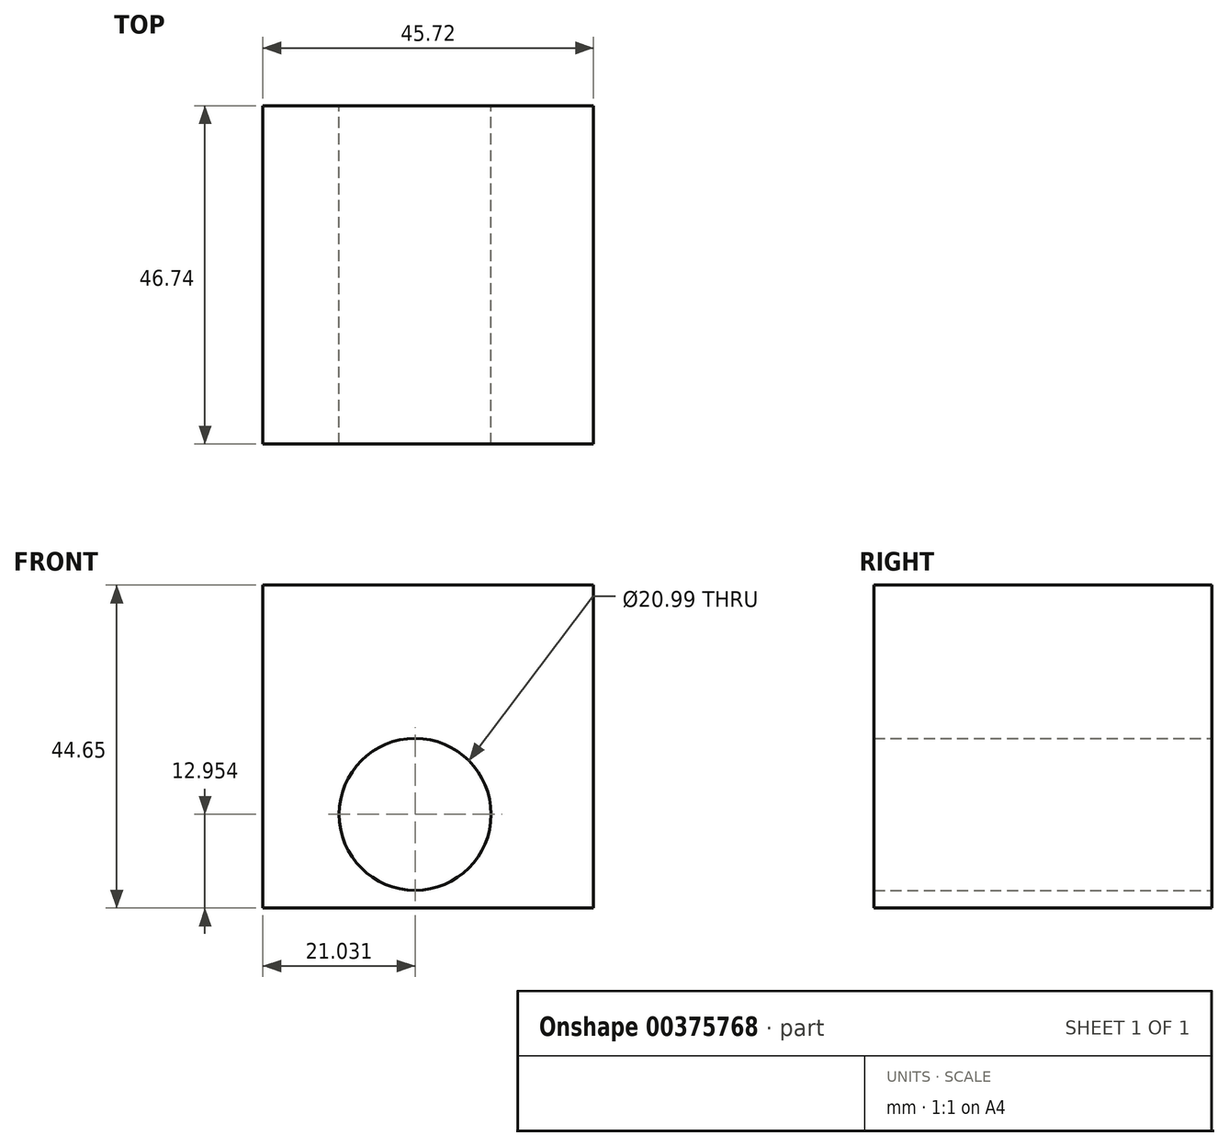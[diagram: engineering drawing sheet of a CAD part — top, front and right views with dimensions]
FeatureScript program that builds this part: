
annotation { "Feature Type Name" : "Feature", "Feature Type Description" : "" }
export const myFeature = defineFeature(function(context is Context, id is Id, definition is map)
    precondition{}
    {
        {
            var Q0;
            Q0=qCreatedBy(makeId("Front.planeOp"),FACE);
            var sketch = newSketch(context, id + "F0", { "sketchPlane" : qUnion([Q0])});
            skLineSegment(sketch, "E0.bottom", {"start": v(0, 44.65) * mm, "end": v(45.72, 44.65) * mm});
            skLineSegment(sketch, "E0.top", {"start": v(0, 0) * mm, "end": v(45.72, 0) * mm});
            skLineSegment(sketch, "E0.left", {"start": v(0, 44.65) * mm, "end": v(0, 0) * mm});
            skLineSegment(sketch, "E0.right", {"start": v(45.72, 44.65) * mm, "end": v(45.72, 0) * mm});
            skCircle(sketch, "E1", {"center": v(21.03, 12.95) * mm, "radius": 10.5 * mm});
            skSolve(sketch);
        }
        {
            var Q0;
            Q0=makeQuery(id+"F0.imprint","IMPRINT",FACE,{"disambiguationData":[TD([[makeQuery(id+"F0.imprint","IMPRINT",EDGE,{"derivedFrom":sQuery(id+"F0.wireOp",EDGE,"E0.bottom")}),-1.0]])]});
            extrude(context, id + "F1", {"entities" : qUnion([Q0]), "depth" : 46.74 * mm});
        }
    });
